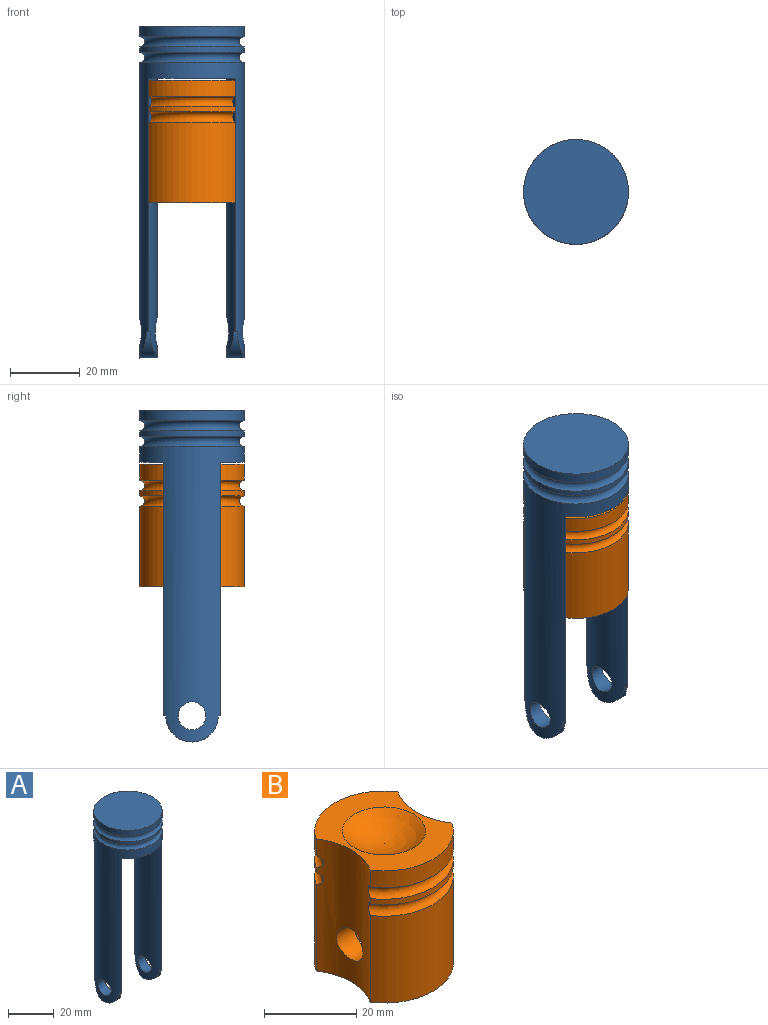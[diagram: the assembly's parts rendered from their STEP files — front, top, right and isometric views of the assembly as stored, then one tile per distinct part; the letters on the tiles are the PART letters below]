
ASSEMBLY  parts=2 mates=1
PART A: 18 faces, bbox 34.8x34.8x95 mm
  f0: cylinder r=15mm len=84.5mm, axis (0,0,-1), area 3053.1mm2, adj f1,f2,f3,f5,f10,f11,f12,f13
  f1: cylinder r=15mm len=80mm, axis (0,0,1), area 1314.5mm2, adj f0,f3,f11,f15,f16,f17
  f2: cylinder r=15mm len=80mm, axis (0,0,1), area 1314.5mm2, adj f0,f3,f10,f12,f13,f14
  f3: plane 30x25mm, normal (0,0,-1), area 339.9mm2, adj f0,f1,f2,f4
  f4: sphere r=14.21mm, area 286.9mm2, adj f3
  f5: torus R=15mm, axis (0,0,1), area 415.9mm2, adj f0,f6
  f6: cylinder r=15mm len=30mm, axis (0,0,-1), area 141.4mm2, adj f5,f7
  f7: torus R=15mm, axis (0,0,1), area 415.9mm2, adj f6,f9
  f8: plane 30x30mm, normal (0,0,1), area 706.9mm2, adj f9
  f9: cylinder r=15mm len=30mm, axis (0,0,-1), area 282.7mm2, adj f7,f8
  f10: cylinder r=4mm len=8mm, axis (-1,0,0), area 112.1mm2, adj f0,f2
  f11: cylinder r=4mm len=8mm, axis (-1,0,0), area 112.1mm2, adj f0,f1
  f12: plane 0.98x0.79mm, normal (0,0,-1), area 0.4mm2, adj f0,f2,f14
  f13: plane 0.98x0.79mm, normal (0,0,-1), area 0.4mm2, adj f0,f2,f14
  f14: cylinder r=7.5mm len=15mm, axis (1,0,0), area 71.3mm2, adj f0,f2,f12,f13
  f15: plane 0.98x0.79mm, normal (0,0,-1), area 0.4mm2, adj f0,f1,f17
  f16: plane 0.98x0.79mm, normal (0,0,-1), area 0.4mm2, adj f0,f1,f17
  f17: cylinder r=7.5mm len=15mm, axis (1,0,0), area 71.3mm2, adj f0,f1,f15,f16
PART B: 28 faces, bbox 30x34.8x35 mm
  f0: cylinder r=15mm len=35mm, axis (0,0,-1), area 548.4mm2, adj f2,f3,f4,f5,f6,f7,f14,f17
  f1: cylinder r=15mm len=35mm, axis (0,0,-1), area 548.4mm2, adj f2,f3,f4,f5,f6,f7,f11,f14
  f2: cylinder r=15mm len=25mm, axis (0,0,-1), area 133mm2, adj f0,f1,f14,f26
  f3: cylinder r=15mm len=25mm, axis (0,0,-1), area 44.3mm2, adj f0,f1,f25,f26
  f4: cylinder r=15mm len=25mm, axis (0,0,-1), area 679.7mm2, adj f0,f1,f17,f25
  f5: cylinder r=15mm len=25mm, axis (0,0,-1), area 133mm2, adj f0,f1,f14,f24
  f6: cylinder r=15mm len=25mm, axis (0,0,-1), area 44.3mm2, adj f0,f1,f23,f24
  f7: cylinder r=15mm len=25mm, axis (0,0,-1), area 679.7mm2, adj f0,f1,f17,f23
  f8: cylinder r=7.5mm len=15mm, axis (-1,0,0), area 17mm2, adj f13,f22
  f9: cylinder r=7.5mm len=15mm, axis (-1,0,0), area 17mm2, adj f13,f22
  f10: cylinder r=7.5mm len=15mm, axis (-1,0,0), area 17mm2, adj f12,f21
  f11: cylinder r=4mm len=8mm, axis (-1,0,0), area 132.5mm2, adj f1,f22
  f12: cylinder r=20mm len=20mm, axis (0,0,1), area 131.8mm2, adj f10,f15,f16,f17,f18,f19
  f13: cylinder r=20mm len=20mm, axis (0,0,1), area 131.8mm2, adj f8,f9,f15,f16,f17,f18
  f14: plane 30x25mm, normal (0,0,1), area 339.9mm2, adj f0,f1,f2,f5,f27
  f15: cylinder r=10mm len=20mm, axis (0,0,1), area 283mm2, adj f12,f13,f17,f18
  f16: cylinder r=10mm len=20mm, axis (0,0,1), area 283mm2, adj f12,f13,f17,f18
  f17: plane 30x25mm, normal (0,0,-1), area 384.6mm2, adj f0,f1,f4,f7,f12,f13,f15,f16
  f18: plane 20x13mm, normal (0,0,-1), area 209.7mm2, adj f12,f13,f15,f16
  f19: cylinder r=7.5mm len=15mm, axis (-1,0,0), area 17mm2, adj f12,f21
  f20: cylinder r=4mm len=8mm, axis (-1,0,0), area 132.5mm2, adj f0,f21
  f21: plane 15x15mm, normal (-1,0,0), area 126.4mm2, adj f10,f19,f20
  f22: plane 15x15mm, normal (1,0,0), area 126.4mm2, adj f8,f9,f11
  f23: torus R=15mm, axis (0,0,1), area 134.7mm2, adj f0,f1,f6,f7
  f24: torus R=15mm, axis (0,0,1), area 134.7mm2, adj f0,f1,f5,f6
  f25: torus R=15mm, axis (0,0,1), area 134.7mm2, adj f0,f1,f3,f4
  f26: torus R=15mm, axis (0,0,1), area 134.7mm2, adj f0,f1,f2,f3
  f27: sphere r=14.21mm, area 286.9mm2, adj f14
PLACE A rot(axis=(0,0,1),0deg) t=(-27.61,-39.02,174.83)mm
PLACE B t=(-27.61,-39.02,159.26)mm
MATE slider B.f15 <-> A.f0  axis (0,0,1) through (-27.61,-39.02,174.26)mm
